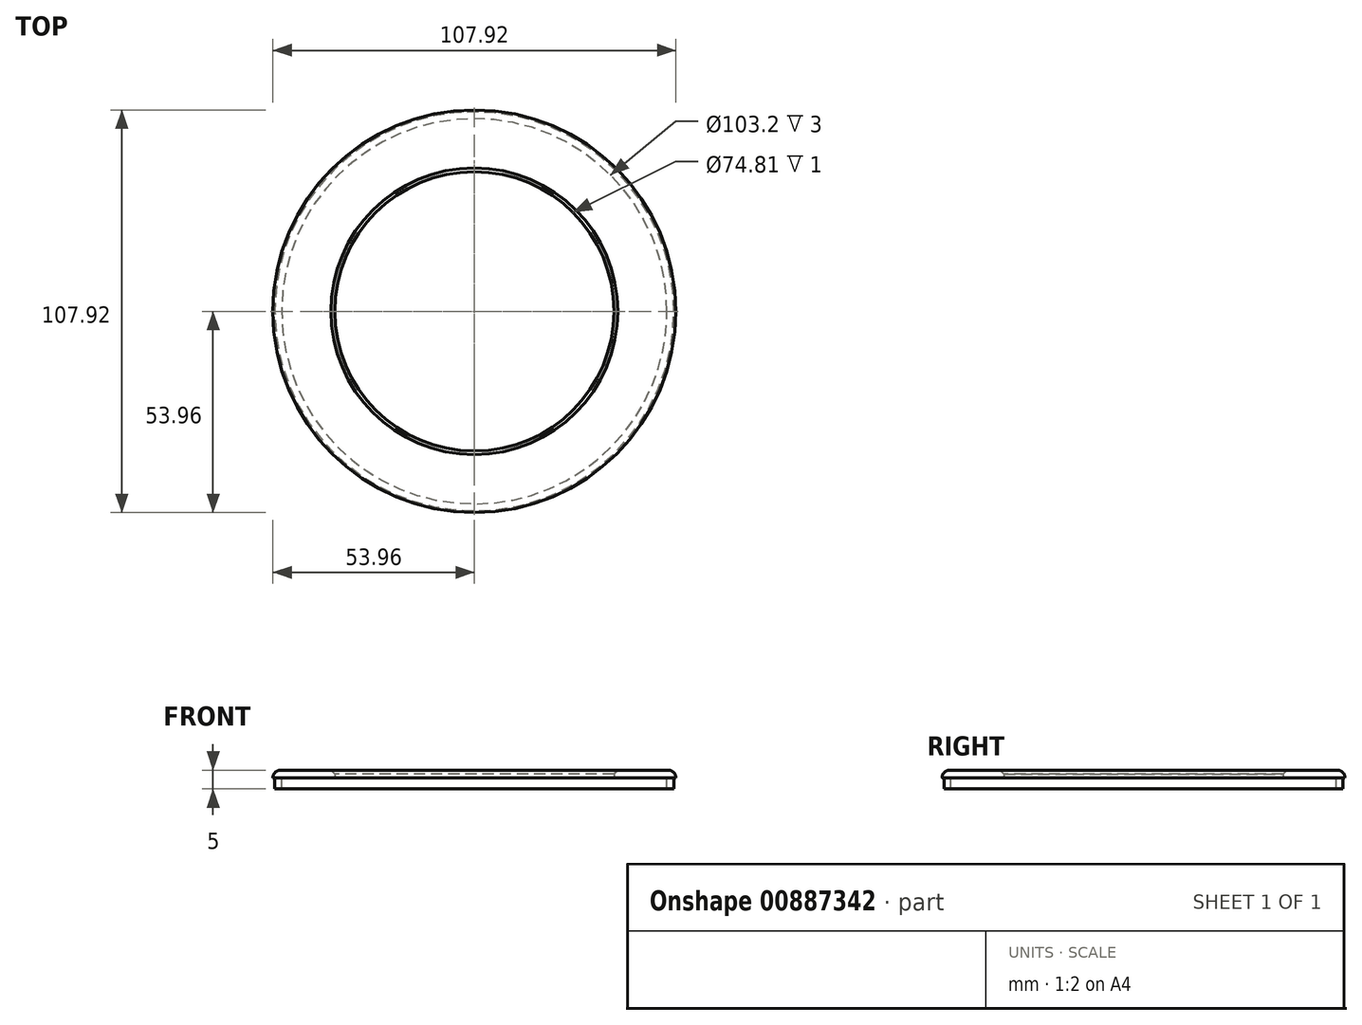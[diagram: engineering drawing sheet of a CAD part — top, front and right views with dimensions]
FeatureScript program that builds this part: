
annotation { "Feature Type Name" : "Feature", "Feature Type Description" : "" }
export const myFeature = defineFeature(function(context is Context, id is Id, definition is map)
    precondition{}
    {
        {
            var Q0;
            Q0=qCreatedBy(makeId("Top.planeOp"),FACE);
            var sketch = newSketch(context, id + "F0", { "sketchPlane" : qUnion([Q0])});
            skCircle(sketch, "E0", {"center": v(0, 0) * mm, "radius": 51.6 * mm});
            skCircle(sketch, "E1", {"center": v(0, 0) * mm, "radius": 53.43 * mm});
            skSolve(sketch);
        }
        {
            var Q0;
            Q0 = qSketchRegion(id + "F0", true);
            extrude(context, id + "F1", {"entities" : qUnion([Q0]), "oppositeDirection" : true, "depth" : 3 * mm, "offsetDistance" : 25 * mm});
        }
        {
            var Q0;
            Q0=makeQuery(id+"F1.opExtrude","CAP_FACE",FACE,{"disambiguationData":[OSD([sQuery(id+"F0.wireOp",EDGE,"E0"),sQuery(id+"F0.wireOp",EDGE,"E1")])],"isStart":true});
            cPlane(context, id + "F2", {"entities" : qUnion([Q0]), "cplaneType" : CPlaneType.OFFSET, "offset" : 0 * mm, "width" : 150 * mm, "height" : 150 * mm});
        }
        {
            var Q0;
            Q0=qCreatedBy(id+"F2.planeOp",FACE);
            var sketch = newSketch(context, id + "F3", { "sketchPlane" : qUnion([Q0])});
            skCircle(sketch, "E2", {"center": v(0, 0) * mm, "radius": 53.96 * mm});
            skSolve(sketch);
        }
        {
            var Q0;
            Q0 = qSketchRegion(id + "F3", true);
            extrude(context, id + "F4", {"entities" : qUnion([Q0]), "operationType" : NewBodyOperationType.ADD, "depth" : 2 * mm, "offsetDistance" : 25 * mm});
        }
        {
            var Q0;
            Q0=makeQuery(id+"F4.opExtrude","CAP_FACE",FACE,{"disambiguationData":[OSD([sQuery(id+"F3.wireOp",EDGE,"E2")])],"isStart":false});
            fillet(context, id + "F5", {"entities" : qUnion([Q0]), "radius" : 2 * mm, "tangentPropagation" : true, "allowEdgeOverflow" : false});
        }
        {
            var Q0;
            Q0=qCreatedBy(id+"F2.planeOp",FACE);
            var sketch = newSketch(context, id + "F6", { "sketchPlane" : qUnion([Q0])});
            skCircle(sketch, "E3", {"center": v(0, 0) * mm, "radius": 37.4 * mm});
            skSolve(sketch);
        }
        {
            var Q0;
            Q0 = qSketchRegion(id + "F6", true);
            extrude(context, id + "F7", {"entities" : qUnion([Q0]), "operationType" : NewBodyOperationType.REMOVE, "depth" : 3 * mm, "offsetDistance" : 25 * mm});
        }
        {
            var Q0;
            Q0=makeQuery(id+"F7.boolean.opBoolean","INTERSECT",EDGE,{"derivedFrom":[makeQuery(id+"F4.opExtrude","CAP_FACE",FACE,{"disambiguationData":[OSD([sQuery(id+"F3.wireOp",EDGE,"E2")])],"isStart":false}),makeQuery(id+"F7.opExtrude","SWEPT_FACE",FACE,{"disambiguationData":[OSD([sQuery(id+"F6.wireOp",EDGE,"E3")])]})]});
            chamfer(context, id + "F8", {"entities" : qUnion([Q0]), "chamferType" : ChamferType.TWO_OFFSETS, "width1" : 1 * mm, "oppositeDirection" : false, "width2" : 1 * mm, "tangentPropagation" : true});
        }
    });
